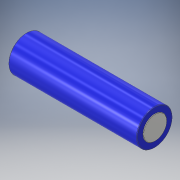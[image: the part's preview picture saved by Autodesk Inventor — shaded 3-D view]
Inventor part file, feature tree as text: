
AUTODESK INVENTOR PART (.ipt)
format: ipt  version: 2019 (Build 230136000, 136)  size: 142,848 bytes
history: native  units: mm
features: fillet x4, extrude x3, sketch x3
ambient origin geometry x8: Origin, YZ Plane, XZ Plane, XY Plane, X Axis, Y Axis, Z Axis, Center Point
bodies: Solid1 (feature_tree)
feature tree (10):
  extrude  "Extrusion1"  Depth=65.0mm TaperAngle=0.0deg
  extrude  "Extrusion2"  Depth=0.2mm TaperAngle=0.0deg
  fillet  "Fillet1"  Radius=0.2mm
  fillet  "Fillet2"  Radius=0.3mm
  fillet  "Fillet3"  Radius=0.3mm
  extrude  "Extrusion3"  Depth=0.7mm TaperAngle=0.0deg
  fillet  "Fillet4"  Radius=0.3mm
  sketch  "Sketch1"  dims[d0=18.0mm d1=65.0mm d2=0.0mm]
  sketch  "Sketch2"  dims[d3=12.0mm d4=0.2mm d5=0.0mm d6=0.2mm d7=0.3mm d8=0.3mm]
  sketch  "Sketch3"  dims[d9=10.0mm d10=0.7mm d11=0.0mm d12=0.3mm]
